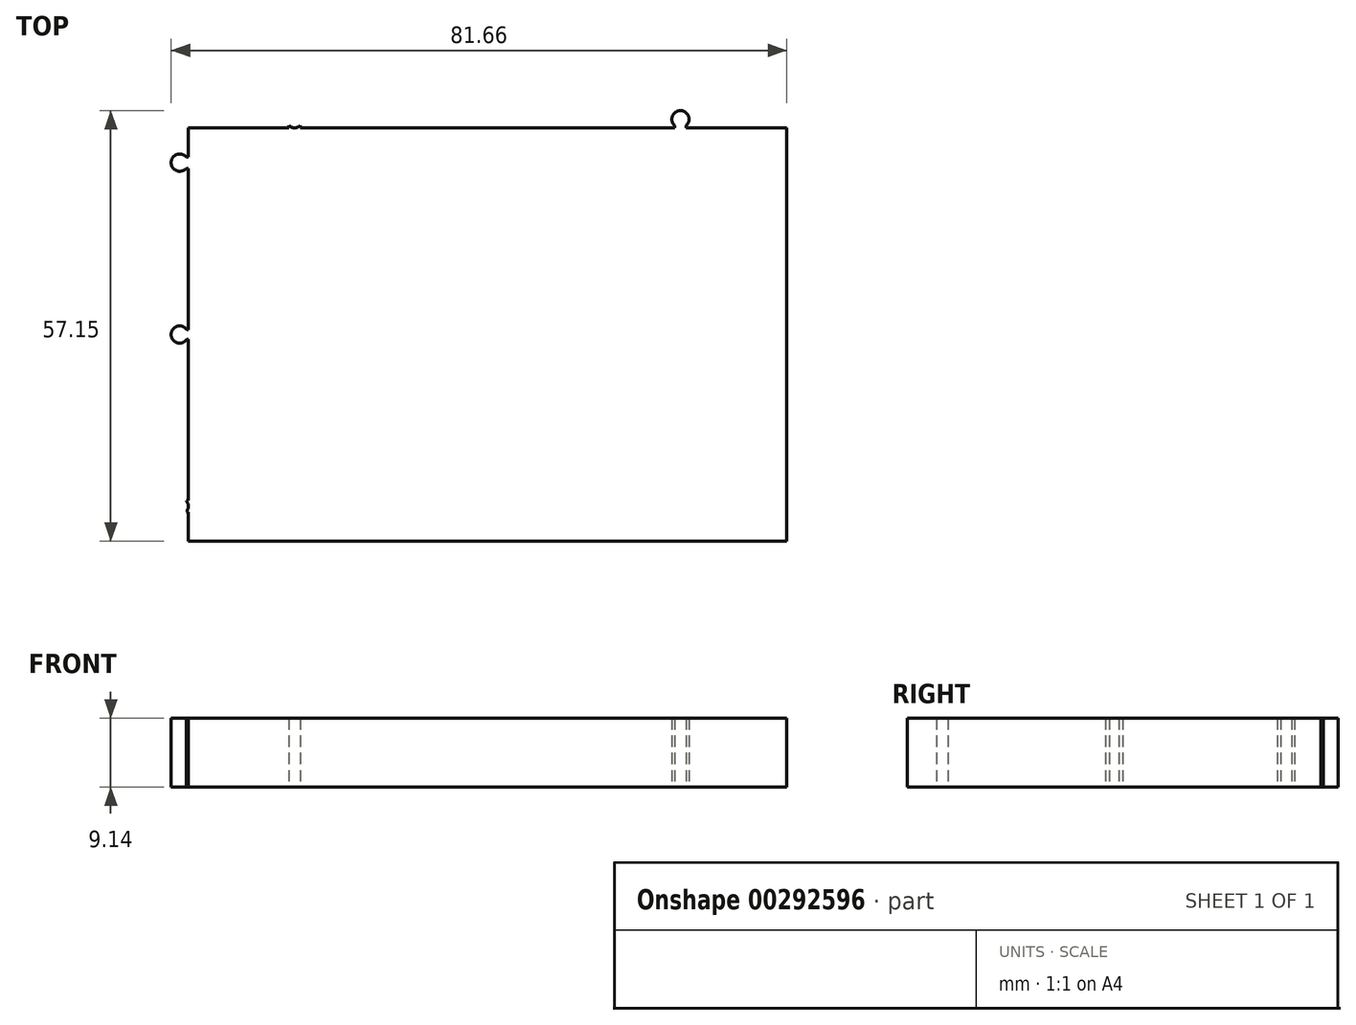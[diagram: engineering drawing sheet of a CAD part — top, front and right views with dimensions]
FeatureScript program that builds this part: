
annotation { "Feature Type Name" : "Feature", "Feature Type Description" : "" }
export const myFeature = defineFeature(function(context is Context, id is Id, definition is map)
    precondition{}
    {
        {
            var Q0;
            Q0=qCreatedBy(makeId("Top.planeOp"),FACE);
            var sketch = newSketch(context, id + "F0", { "sketchPlane" : qUnion([Q0])});
            skLineSegment(sketch, "E0.bottom", {"start": v(-39.69, 27.43) * mm, "end": v(39.69, 27.43) * mm});
            skLineSegment(sketch, "E0.top", {"start": v(-39.69, -27.43) * mm, "end": v(39.69, -27.43) * mm});
            skLineSegment(sketch, "E0.left", {"start": v(-39.69, 27.43) * mm, "end": v(-39.69, -27.43) * mm});
            skLineSegment(sketch, "E0.right", {"start": v(39.69, 27.43) * mm, "end": v(39.69, -27.43) * mm});
            skLineSegment(sketch, "E1", {"start": v(0, 0) * mm, "end": v(0, 27.43) * mm, "construction": true});
            skLineSegment(sketch, "E2", {"start": v(0, 0) * mm, "end": v(0, -27.43) * mm, "construction": true});
            skLineSegment(sketch, "E3", {"start": v(-39.69, 0) * mm, "end": v(0, 0) * mm, "construction": true});
            skLineSegment(sketch, "E4", {"start": v(39.69, 0) * mm, "end": v(0, 0) * mm, "construction": true});
            skCircle(sketch, "E5", {"center": v(25.6, 28.58) * mm, "radius": 1.14 * mm});
            skLineSegment(sketch, "E6", {"start": v(39.69, 27.43) * mm, "end": v(39.69, 28.9) * mm, "construction": true});
            skLineSegment(sketch, "E7", {"start": v(24.45, 28.57) * mm, "end": v(39.69, 28.57) * mm, "construction": true});
            skCircle(sketch, "E8.MirrorC", {"center": v(-25.6, 28.58) * mm, "radius": 1.14 * mm});
            skCircle(sketch, "E9", {"center": v(-40.83, 22.8) * mm, "radius": 1.14 * mm});
            skLineSegment(sketch, "E10", {"start": v(-39.69, 27.43) * mm, "end": v(-54.1, 27.43) * mm, "construction": true});
            skLineSegment(sketch, "E11", {"start": v(-40.83, 21.67) * mm, "end": v(-40.83, 27.43) * mm, "construction": true});
            skPoint(sketch, "E11.endSnap0", {"position": v(-46.9, 27.43) * mm});
            skCircle(sketch, "E12.MirrorC", {"center": v(-40.83, -22.8) * mm, "radius": 1.14 * mm});
            skCircle(sketch, "E13", {"center": v(-40.83, 0) * mm, "radius": 1.14 * mm});
            skLineSegment(sketch, "E14", {"start": v(25.6, 28.58) * mm, "end": v(25.6, 27.43) * mm, "construction": true});
            skLineSegment(sketch, "E15", {"start": v(24.81, 27.74) * mm, "end": v(24.81, 27.43) * mm});
            skLineSegment(sketch, "E16.MirrorCS", {"start": v(26.37, 27.74) * mm, "end": v(26.37, 27.43) * mm});
            skLineSegment(sketch, "E17.MirrorCS", {"start": v(-24.81, 27.74) * mm, "end": v(-24.81, 27.43) * mm});
            skLineSegment(sketch, "E18.MirrorCS", {"start": v(-26.37, 27.74) * mm, "end": v(-26.37, 27.43) * mm});
            skLineSegment(sketch, "E19", {"start": v(-40.83, 22.8) * mm, "end": v(-39.69, 22.8) * mm, "construction": true});
            skLineSegment(sketch, "E20", {"start": v(-39.97, 23.56) * mm, "end": v(-39.69, 23.56) * mm});
            skLineSegment(sketch, "E21.MirrorCS", {"start": v(-39.97, 22.05) * mm, "end": v(-39.69, 22.05) * mm});
            skLineSegment(sketch, "E22.MirrorCS", {"start": v(-39.97, -23.56) * mm, "end": v(-39.69, -23.56) * mm});
            skLineSegment(sketch, "E23.MirrorCS", {"start": v(-39.97, -22.05) * mm, "end": v(-39.69, -22.05) * mm});
            skLineSegment(sketch, "E24", {"start": v(-40.83, 0) * mm, "end": v(-39.69, 0) * mm, "construction": true});
            skLineSegment(sketch, "E25", {"start": v(-39.87, 0.62) * mm, "end": v(-39.69, 0.62) * mm});
            skLineSegment(sketch, "E26.MirrorCS", {"start": v(-39.87, -0.62) * mm, "end": v(-39.69, -0.62) * mm});
            skSolve(sketch);
        }
        {
            var Q0;
            {var subQ5=sQuery(id+"F0.wireOp",EDGE,"E0.top");Q0=makeQuery(id+"F0.imprint","IMPRINT",FACE,{"disambiguationData":[TD([[makeQuery(id+"F0.imprint","IMPRINT",EDGE,{"derivedFrom":subQ5}),1.0]])]});}
            var Q1;
            {var subQ0=sQuery(id+"F0.wireOp",EDGE,"E18.MirrorCS");Q1=makeQuery(id+"F0.imprint","IMPRINT",FACE,{"disambiguationData":[TD([[makeQuery(id+"F0.imprint","IMPRINT",EDGE,{"derivedFrom":subQ0}),1.0]])]});}
            var Q2;
            {var subQ0=sQuery(id+"F0.wireOp",EDGE,"E13");var subQ1=makeQuery(id+"F0.imprint","INTERSECT",VERTEX,{"derivedFrom":[subQ0,sQuery(id+"F0.wireOp",EDGE,"E25")]});Q2=makeQuery(id+"F0.imprint","IMPRINT",FACE,{"disambiguationData":[TD([[makeQuery(id+"F0.imprint","IMPRINT",EDGE,{"disambiguationData":[TD([[subQ1,1.0]])],"derivedFrom":subQ0}),1.0]])]});}
            var Q3;
            {var subQ0=sQuery(id+"F0.wireOp",EDGE,"E12.MirrorC");var subQ1=makeQuery(id+"F0.imprint","INTERSECT",VERTEX,{"derivedFrom":[subQ0,sQuery(id+"F0.wireOp",EDGE,"E22.MirrorCS")]});Q3=makeQuery(id+"F0.imprint","IMPRINT",FACE,{"disambiguationData":[TD([[makeQuery(id+"F0.imprint","IMPRINT",EDGE,{"disambiguationData":[TD([[subQ1,1.0]])],"derivedFrom":subQ0}),-1.0]])]});}
            var Q4;
            {var subQ0=sQuery(id+"F0.wireOp",EDGE,"E5");var subQ1=makeQuery(id+"F0.imprint","INTERSECT",VERTEX,{"derivedFrom":[subQ0,sQuery(id+"F0.wireOp",EDGE,"E15")]});Q4=makeQuery(id+"F0.imprint","IMPRINT",FACE,{"disambiguationData":[TD([[makeQuery(id+"F0.imprint","IMPRINT",EDGE,{"disambiguationData":[TD([[subQ1,-1.0]])],"derivedFrom":subQ0}),1.0]])]});}
            var Q5;
            {var subQ0=sQuery(id+"F0.wireOp",EDGE,"E17.MirrorCS");Q5=makeQuery(id+"F0.imprint","IMPRINT",FACE,{"disambiguationData":[TD([[makeQuery(id+"F0.imprint","IMPRINT",EDGE,{"derivedFrom":subQ0}),-1.0]])]});}
            var Q6;
            {var subQ0=sQuery(id+"F0.wireOp",EDGE,"E8.MirrorC");var subQ1=makeQuery(id+"F0.imprint","INTERSECT",VERTEX,{"derivedFrom":[subQ0,sQuery(id+"F0.wireOp",EDGE,"E17.MirrorCS")]});Q6=makeQuery(id+"F0.imprint","IMPRINT",FACE,{"disambiguationData":[TD([[makeQuery(id+"F0.imprint","IMPRINT",EDGE,{"disambiguationData":[TD([[subQ1,-1.0]])],"derivedFrom":subQ0}),-1.0]])]});}
            var Q7;
            {var subQ0=sQuery(id+"F0.wireOp",EDGE,"E20");Q7=makeQuery(id+"F0.imprint","IMPRINT",FACE,{"disambiguationData":[TD([[makeQuery(id+"F0.imprint","IMPRINT",EDGE,{"derivedFrom":subQ0}),-1.0]])]});}
            var Q8;
            {var subQ0=sQuery(id+"F0.wireOp",EDGE,"E15");Q8=makeQuery(id+"F0.imprint","IMPRINT",FACE,{"disambiguationData":[TD([[makeQuery(id+"F0.imprint","IMPRINT",EDGE,{"derivedFrom":subQ0}),1.0]])]});}
            var Q9;
            {var subQ0=sQuery(id+"F0.wireOp",EDGE,"E16.MirrorCS");Q9=makeQuery(id+"F0.imprint","IMPRINT",FACE,{"disambiguationData":[TD([[makeQuery(id+"F0.imprint","IMPRINT",EDGE,{"derivedFrom":subQ0}),-1.0]])]});}
            var Q10;
            {var subQ0=sQuery(id+"F0.wireOp",EDGE,"E23.MirrorCS");Q10=makeQuery(id+"F0.imprint","IMPRINT",FACE,{"disambiguationData":[TD([[makeQuery(id+"F0.imprint","IMPRINT",EDGE,{"derivedFrom":subQ0}),-1.0]])]});}
            var Q11;
            {var subQ0=sQuery(id+"F0.wireOp",EDGE,"E22.MirrorCS");Q11=makeQuery(id+"F0.imprint","IMPRINT",FACE,{"disambiguationData":[TD([[makeQuery(id+"F0.imprint","IMPRINT",EDGE,{"derivedFrom":subQ0}),1.0]])]});}
            var Q12;
            {var subQ0=sQuery(id+"F0.wireOp",EDGE,"E9");var subQ1=makeQuery(id+"F0.imprint","INTERSECT",VERTEX,{"derivedFrom":[subQ0,sQuery(id+"F0.wireOp",EDGE,"E20")]});Q12=makeQuery(id+"F0.imprint","IMPRINT",FACE,{"disambiguationData":[TD([[makeQuery(id+"F0.imprint","IMPRINT",EDGE,{"disambiguationData":[TD([[subQ1,1.0]])],"derivedFrom":subQ0}),1.0]])]});}
            var Q13;
            {var subQ0=sQuery(id+"F0.wireOp",EDGE,"E26.MirrorCS");Q13=makeQuery(id+"F0.imprint","IMPRINT",FACE,{"disambiguationData":[TD([[makeQuery(id+"F0.imprint","IMPRINT",EDGE,{"derivedFrom":subQ0}),1.0]])]});}
            var Q14;
            {var subQ0=sQuery(id+"F0.wireOp",EDGE,"E21.MirrorCS");Q14=makeQuery(id+"F0.imprint","IMPRINT",FACE,{"disambiguationData":[TD([[makeQuery(id+"F0.imprint","IMPRINT",EDGE,{"derivedFrom":subQ0}),1.0]])]});}
            var Q15;
            {var subQ0=sQuery(id+"F0.wireOp",EDGE,"E25");Q15=makeQuery(id+"F0.imprint","IMPRINT",FACE,{"disambiguationData":[TD([[makeQuery(id+"F0.imprint","IMPRINT",EDGE,{"derivedFrom":subQ0}),-1.0]])]});}
            extrude(context, id + "F1", {"entities" : qUnion([Q0, Q1, Q2, Q3, Q4, Q5, Q6, Q7, Q8, Q9, Q10, Q11, Q12, Q13, Q14, Q15]), "depth" : 9.14 * mm});
        }
    });
